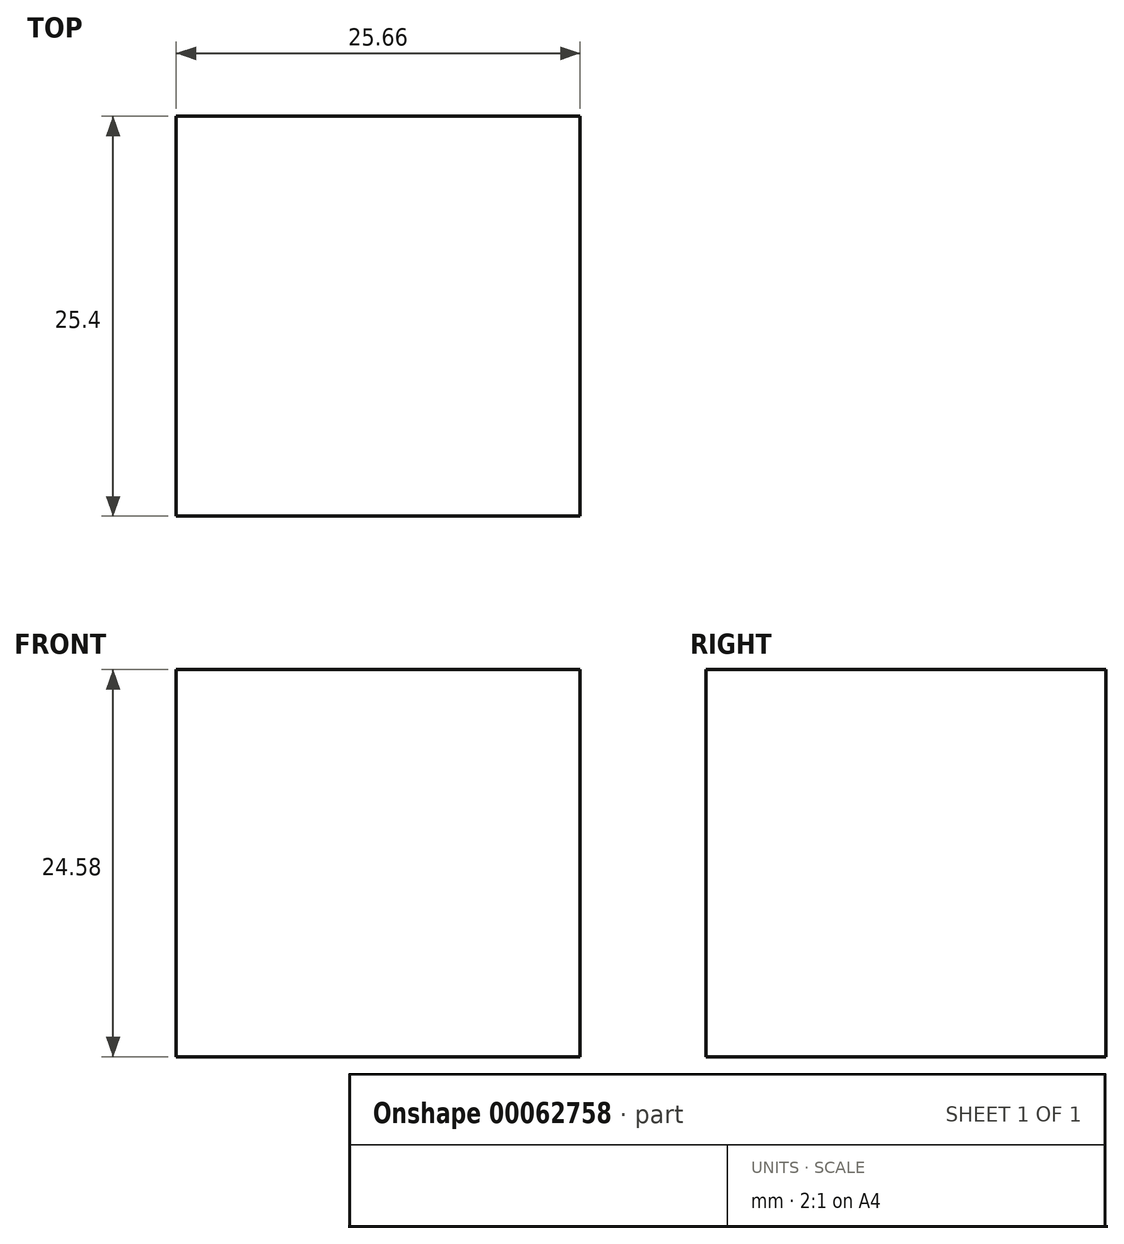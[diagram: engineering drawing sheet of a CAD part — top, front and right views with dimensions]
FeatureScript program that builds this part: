
annotation { "Feature Type Name" : "Feature", "Feature Type Description" : "" }
export const myFeature = defineFeature(function(context is Context, id is Id, definition is map)
    precondition{}
    {
        {
            var Q0;
            Q0=qCreatedBy(makeId("Front.planeOp"),FACE);
            var sketch = newSketch(context, id + "F0", { "sketchPlane" : qUnion([Q0])});
            skLineSegment(sketch, "E0", {"start": v(-61.3, 42.6) * mm, "end": v(-61.3, 18.02) * mm});
            skLineSegment(sketch, "E1", {"start": v(-61.3, 18.02) * mm, "end": v(-35.64, 18.02) * mm});
            skLineSegment(sketch, "E2", {"start": v(-35.64, 18.02) * mm, "end": v(-35.64, 42.6) * mm});
            skLineSegment(sketch, "E3", {"start": v(-35.64, 42.6) * mm, "end": v(-61.3, 42.6) * mm});
            skSolve(sketch);
        }
        {
            var Q0;
            Q0=makeQuery(id+"F0.imprint","IMPRINT",FACE,{"disambiguationData":[TD([[makeQuery(id+"F0.imprint","IMPRINT",EDGE,{"derivedFrom":sQuery(id+"F0.wireOp",EDGE,"E0")}),1.0]])]});
            extrude(context, id + "F1", {"entities" : qUnion([Q0]), "depth" : 25.4 * mm});
        }
    });
